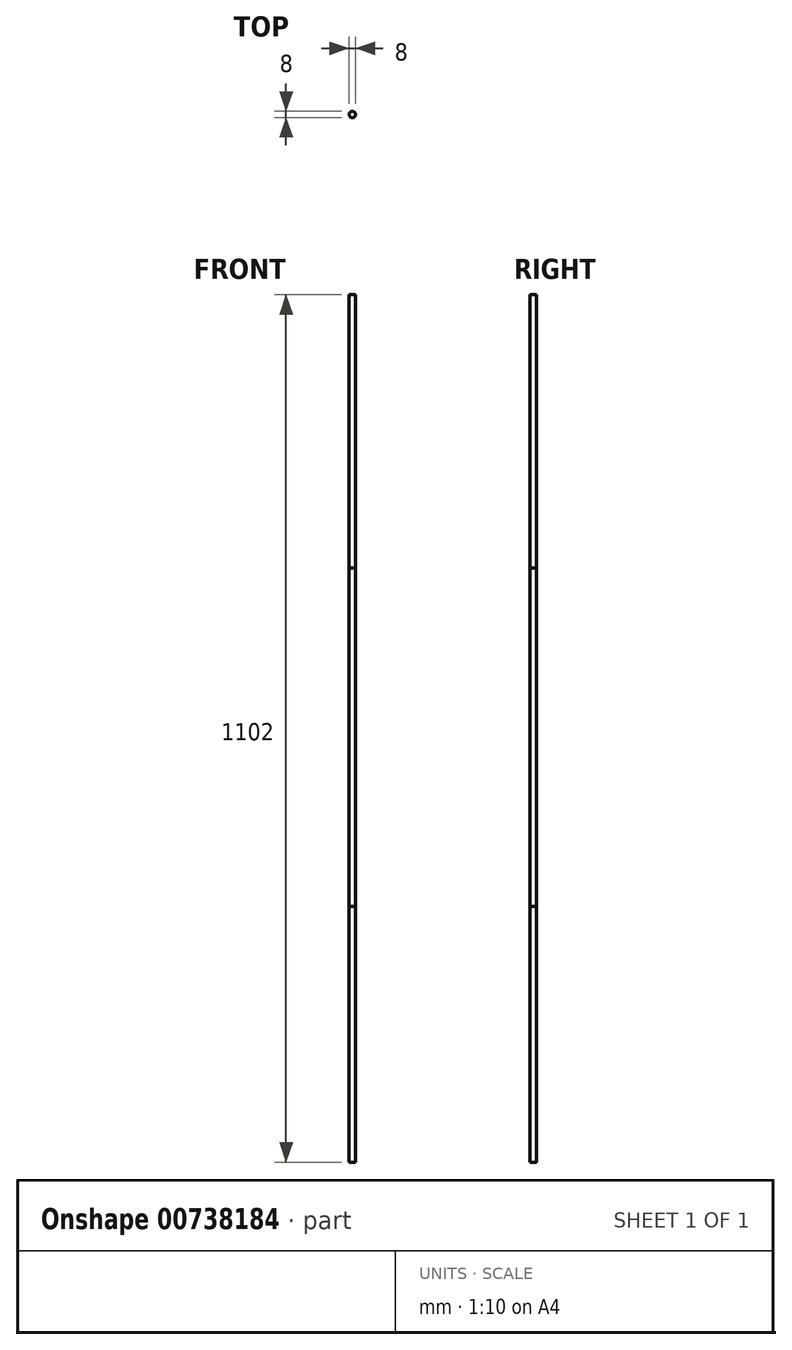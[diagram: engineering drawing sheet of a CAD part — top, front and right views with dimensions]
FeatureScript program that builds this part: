
annotation { "Feature Type Name" : "Feature", "Feature Type Description" : "" }
export const myFeature = defineFeature(function(context is Context, id is Id, definition is map)
    precondition{}
    {
        {
            var Q0;
            Q0=qCreatedBy(makeId("Top.planeOp"),FACE);
            var sketch = newSketch(context, id + "F0", { "sketchPlane" : qUnion([Q0])});
            skCircle(sketch, "E0", {"center": v(0, 0) * mm, "radius": 4 * mm});
            skSolve(sketch);
        }
        {
            var Q0;
            Q0=makeQuery(id+"F0.imprint","IMPRINT",FACE,{"disambiguationData":[TD([[makeQuery(id+"F0.imprint","IMPRINT",EDGE,{"derivedFrom":sQuery(id+"F0.wireOp",EDGE,"E0")}),1.0]])]});
            extrude(context, id + "F1", {"entities" : qUnion([Q0]), "depth" : 430 * mm, "offsetDistance" : 25 * mm});
        }
        {
            var Q0;
            Q0=makeQuery(id+"F1.opExtrude","CAP_FACE",FACE,{"disambiguationData":[OSD([sQuery(id+"F0.wireOp",EDGE,"E0")])],"isStart":false});
            extrude(context, id + "F2", {"entities" : qUnion([Q0]), "depth" : 347 * mm, "offsetDistance" : 25 * mm});
        }
        {
            var Q0;
            Q0=makeQuery(id+"F1.opExtrude","CAP_FACE",FACE,{"disambiguationData":[OSD([sQuery(id+"F0.wireOp",EDGE,"E0")])],"isStart":true});
            extrude(context, id + "F3", {"entities" : qUnion([Q0]), "depth" : 325 * mm, "offsetDistance" : 25 * mm});
        }
    });
